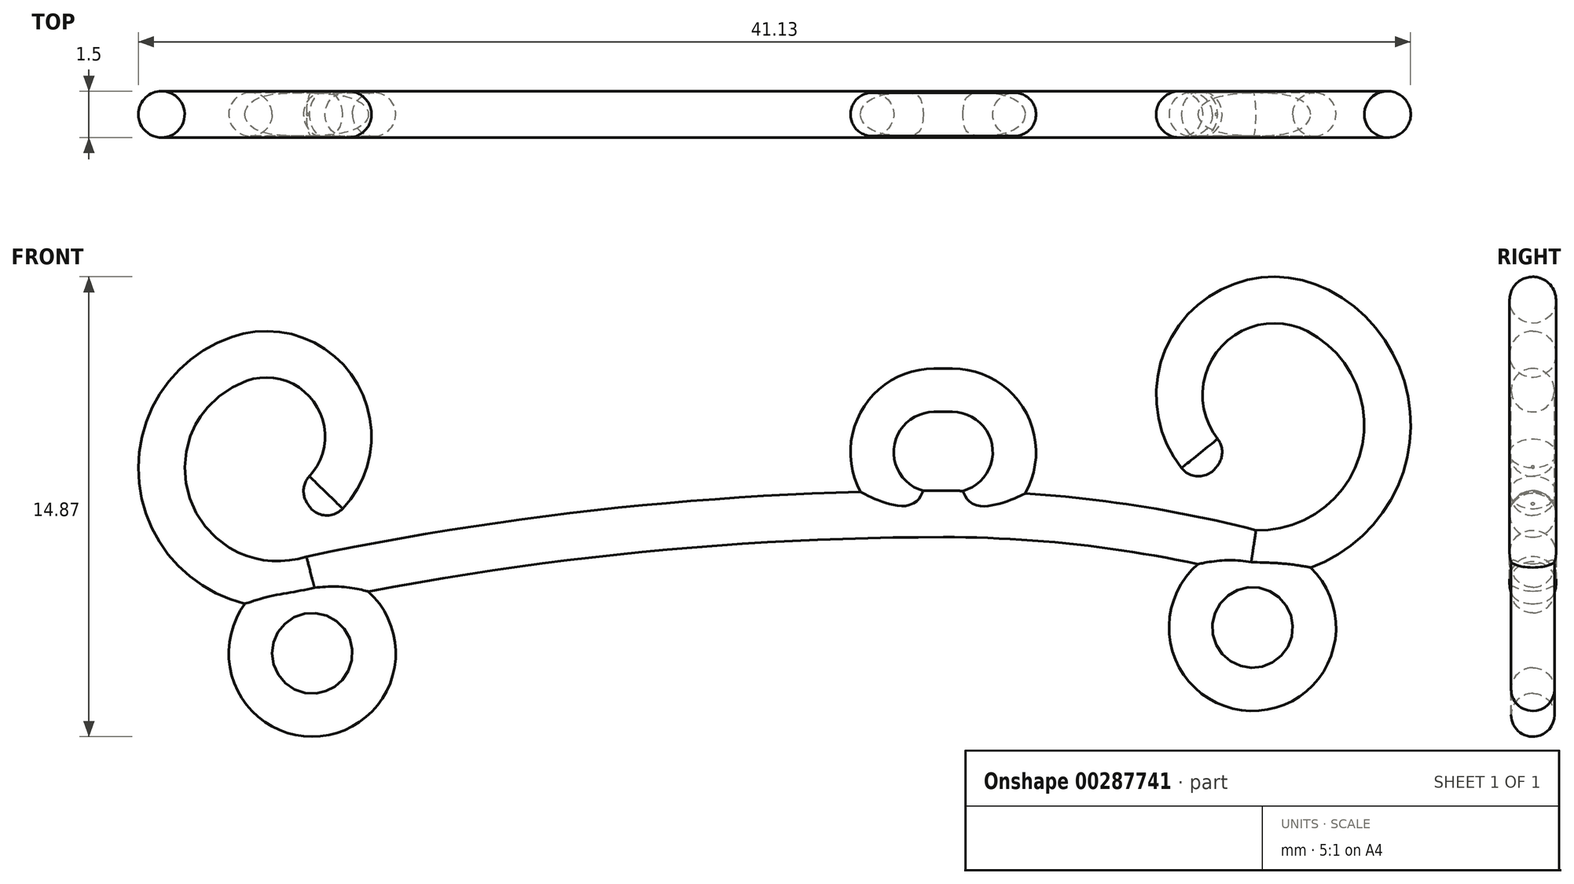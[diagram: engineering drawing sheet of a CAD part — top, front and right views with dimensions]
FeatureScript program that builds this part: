
annotation { "Feature Type Name" : "Feature", "Feature Type Description" : "" }
export const myFeature = defineFeature(function(context is Context, id is Id, definition is map)
    precondition{}
    {
        {
            var Q0;
            Q0=qCreatedBy(makeId("Front.planeOp"),FACE);
            var sketch = newSketch(context, id + "F0", { "sketchPlane" : qUnion([Q0])});
            skLineSegment(sketch, "E0", {"start": v(-0.3, 2) * mm, "end": v(0.3, 2) * mm});
            skArc(sketch, "E1", {"start": v(0.3, 2) * mm, "mid": v(1.71, 1.41) * mm, "end": v(2.3, 0) * mm});
            skArc(sketch, "E2", {"start": v(-0.3, 2) * mm, "mid": v(-2.3, 0) * mm, "end": v(-0.3, -2) * mm});
            skLineSegment(sketch, "E3", {"start": v(-0.3, -2) * mm, "end": v(0.3, -2) * mm});
            skLineSegment(sketch, "E4", {"start": v(0, 1.7) * mm, "end": v(0, -1.12) * mm, "construction": true});
            skArc(sketch, "E5", {"start": v(2.3, 0) * mm, "mid": v(1.71, -1.41) * mm, "end": v(0.3, -2) * mm});
            skSolve(sketch);
        }
        {
            var Q0;
            Q0=qCreatedBy(makeId("Top.planeOp"),FACE);
            var sketch = newSketch(context, id + "F1", { "sketchPlane" : qUnion([Q0])});
            skLineSegment(sketch, "E6", {"start": v(0, 1.94) * mm, "end": v(0, -2.17) * mm, "construction": true});
            skCircle(sketch, "E7", {"center": v(2.3, 0) * mm, "radius": 0.7 * mm});
            skSolve(sketch);
        }
        {
            var Q0;
            Q0=makeQuery(id+"F1.imprint","IMPRINT",FACE,{"disambiguationData":[TD([[makeQuery(id+"F1.imprint","IMPRINT",EDGE,{"derivedFrom":sQuery(id+"F1.wireOp",EDGE,"E7")}),1.0]])]});
            var Q1;
            Q1=sQuery(id+"F0.wireOp",EDGE,"E1");
            var Q2;
            Q2=sQuery(id+"F0.wireOp",EDGE,"E0");
            var Q3;
            Q3=sQuery(id+"F0.wireOp",EDGE,"E2");
            var Q4;
            Q4=sQuery(id+"F0.wireOp",EDGE,"E3");
            var Q5;
            Q5=sQuery(id+"F0.wireOp",EDGE,"E5");
            sweep(context, id + "F2", {"profiles" : qUnion([Q0]), "path" : qUnion([Q1, Q2, Q3, Q4, Q5])});
        }
        {
            var Q0;
            Q0=qCreatedBy(makeId("Right.planeOp"),FACE);
            var sketch = newSketch(context, id + "F3", { "sketchPlane" : qUnion([Q0])});
            skCircle(sketch, "E8", {"center": v(0, -2) * mm, "radius": 0.75 * mm});
            skSolve(sketch);
        }
        {
            var Q0;
            Q0=qCreatedBy(makeId("Front.planeOp"),FACE);
            var sketch = newSketch(context, id + "F4", { "sketchPlane" : qUnion([Q0])});
            skArc(sketch, "E9", {"start": v(-20.4, -4.1) * mm, "mid": v(-25.08, -1.7) * mm, "end": v(-22.76, 3.01) * mm});
            skArc(sketch, "E10", {"start": v(-22.76, 3.01) * mm, "mid": v(-19.5, 1.65) * mm, "end": v(-20.5, -1.75) * mm});
            skArc(sketch, "E11", {"start": v(10, -3.27) * mm, "mid": v(14.22, -0.2) * mm, "end": v(12.11, 4.58) * mm});
            skArc(sketch, "E12", {"start": v(12.11, 4.58) * mm, "mid": v(8.13, 3.52) * mm, "end": v(8.78, -0.54) * mm});
            skArc(sketch, "E13", {"start": v(0, -2) * mm, "mid": v(-10.25, -2.53) * mm, "end": v(-20.4, -4.1) * mm});
            skArc(sketch, "E14", {"start": v(0, -2) * mm, "mid": v(5.04, -2.32) * mm, "end": v(10, -3.27) * mm});
            skSolve(sketch);
        }
        {
            var Q0;
            Q0=makeQuery(id+"F3.imprint","IMPRINT",FACE,{"disambiguationData":[TD([[makeQuery(id+"F3.imprint","IMPRINT",EDGE,{"derivedFrom":sQuery(id+"F3.wireOp",EDGE,"E8")}),1.0]])]});
            var Q1;
            Q1=sQuery(id+"F4.wireOp",EDGE,"E14");
            var Q2;
            Q2=sQuery(id+"F4.wireOp",EDGE,"E11");
            var Q3;
            Q3=sQuery(id+"F4.wireOp",EDGE,"E12");
            sweep(context, id + "F5", {"operationType" : NewBodyOperationType.ADD, "profiles" : qUnion([Q0]), "path" : qUnion([Q1, Q2, Q3])});
        }
        {
            var Q0;
            Q0=makeQuery(id+"F3.imprint","IMPRINT",FACE,{"disambiguationData":[TD([[makeQuery(id+"F3.imprint","IMPRINT",EDGE,{"derivedFrom":sQuery(id+"F3.wireOp",EDGE,"E8")}),1.0]])]});
            var Q1;
            Q1=sQuery(id+"F3.wireOp",EDGE,"E8");
            var Q2;
            Q2=sQuery(id+"F4.wireOp",EDGE,"E13");
            var Q3;
            Q3=sQuery(id+"F4.wireOp",EDGE,"E9");
            var Q4;
            Q4=sQuery(id+"F4.wireOp",EDGE,"E10");
            sweep(context, id + "F6", {"operationType" : NewBodyOperationType.ADD, "profiles" : qUnion([Q0]), "surfaceProfiles" : qUnion([Q1]), "path" : qUnion([Q2, Q3, Q4])});
        }
        {
            var Q0;
            Q0=qCreatedBy(makeId("Front.planeOp"),FACE);
            var sketch = newSketch(context, id + "F7", { "sketchPlane" : qUnion([Q0])});
            skPoint(sketch, "E15", {"position": v(10, -5.67) * mm});
            skPoint(sketch, "E16", {"position": v(-20.4, -6.5) * mm});
            skLineSegment(sketch, "E17", {"start": v(0, 0) * mm, "end": v(15.34, 0) * mm});
            skLineSegment(sketch, "E18", {"start": v(0, 0) * mm, "end": v(0, -9.1) * mm});
            skSolve(sketch);
        }
        {
            var Q0;
            Q0=qCreatedBy(makeId("Top.planeOp"),FACE);
            var Q1;
            Q1=sQuery(id+"F7.wireOp",VERTEX,"E15");
            cPlane(context, id + "F8", {"entities" : qUnion([Q0, Q1]), "cplaneType" : CPlaneType.PLANE_POINT, "offset" : 25 * mm, "width" : 150 * mm, "height" : 150 * mm});
        }
        {
            var Q0;
            Q0=qCreatedBy(makeId("Top.planeOp"),FACE);
            var Q1;
            Q1=sQuery(id+"F7.wireOp",VERTEX,"E16");
            cPlane(context, id + "F9", {"entities" : qUnion([Q0, Q1]), "cplaneType" : CPlaneType.PLANE_POINT, "offset" : 25 * mm, "width" : 150 * mm, "height" : 150 * mm});
        }
        {
            var Q0;
            Q0=qCreatedBy(id+"F8.planeOp",FACE);
            var sketch = newSketch(context, id + "F10", { "sketchPlane" : qUnion([Q0])});
            skLineSegment(sketch, "E19", {"start": v(10, 0) * mm, "end": v(10, -3.23) * mm, "construction": true});
            skCircle(sketch, "E20", {"center": v(12, 0) * mm, "radius": 0.7 * mm});
            skSolve(sketch);
        }
        {
            var Q0;
            Q0=makeQuery(id+"F10.imprint","IMPRINT",FACE,{"disambiguationData":[TD([[makeQuery(id+"F10.imprint","IMPRINT",EDGE,{"derivedFrom":sQuery(id+"F10.wireOp",EDGE,"E20")}),1.0]])]});
            var Q1;
            Q1=sQuery(id+"F10.wireOp",EDGE,"E19");
            revolve(context, id + "F11", {"operationType" : NewBodyOperationType.ADD, "entities" : qUnion([Q0]), "axis" : qUnion([Q1]), "revolveType" : RevolveType.FULL});
        }
        {
            var Q0;
            Q0=qCreatedBy(id+"F9.planeOp",FACE);
            var sketch = newSketch(context, id + "F12", { "sketchPlane" : qUnion([Q0])});
            skLineSegment(sketch, "E21", {"start": v(-20.4, 0) * mm, "end": v(-20.4, -1.79) * mm, "construction": true});
            skCircle(sketch, "E22", {"center": v(-22.4, 0) * mm, "radius": 0.7 * mm});
            skSolve(sketch);
        }
        {
            var Q0;
            Q0=qSketchRegion(id+"F12",true);
            var Q1;
            Q1=sQuery(id+"F12.wireOp",EDGE,"E21");
            revolve(context, id + "F13", {"operationType" : NewBodyOperationType.ADD, "entities" : qUnion([Q0]), "axis" : qUnion([Q1]), "revolveType" : RevolveType.FULL});
        }
        {
            var Q0;
            Q0=makeQuery(id+"F6.opSweep","CAP_EDGE",EDGE,{"disambiguationData":[OSD([sQuery(id+"F3.wireOp",EDGE,"E8"),sQuery(id+"F4.wireOp",VERTEX,"E10.end")])],"isStart":false});
            var Q1;
            Q1=makeQuery(id+"F5.opSweep","CAP_EDGE",EDGE,{"disambiguationData":[OSD([sQuery(id+"F3.wireOp",EDGE,"E8"),sQuery(id+"F4.wireOp",VERTEX,"E12.end")])],"isStart":false});
            fillet(context, id + "F14", {"entities" : qUnion([Q0, Q1]), "radius" : 0.7 * mm, "tangentPropagation" : true, "allowEdgeOverflow" : false});
        }
        {
            var Q0;
            Q0=qCreatedBy(makeId("Right.planeOp"),FACE);
            var Q1;
            Q1=sQuery(id+"F10.wireOp",EDGE,"E19");
            cPlane(context, id + "F15", {"entities" : qUnion([Q0, Q1]), "cplaneType" : CPlaneType.LINE_ANGLE, "offset" : 25 * mm, "angle" : 15 * degree, "oppositeDirection" : true, "width" : 150 * mm, "height" : 150 * mm});
        }
        {
            var Q0;
            Q0=qCreatedBy(id+"F15.planeOp",FACE);
            var sketch = newSketch(context, id + "F16", { "sketchPlane" : qUnion([Q0])});
            skLineSegment(sketch, "E23", {"start": v(-0.7, -6.87) * mm, "end": v(-0.7, -3.81) * mm});
            skLineSegment(sketch, "E24", {"start": v(0.7, -6.87) * mm, "end": v(0.7, -3.73) * mm});
            skArc(sketch, "E25", {"start": v(-0.29, -4.25) * mm, "mid": v(0, -5.59) * mm, "end": v(0.29, -4.25) * mm});
            skArc(sketch, "E26", {"start": v(0.06, -1.59) * mm, "mid": v(0, -0.19) * mm, "end": v(-0.06, -1.59) * mm});
            skSolve(sketch);
        }
    });
